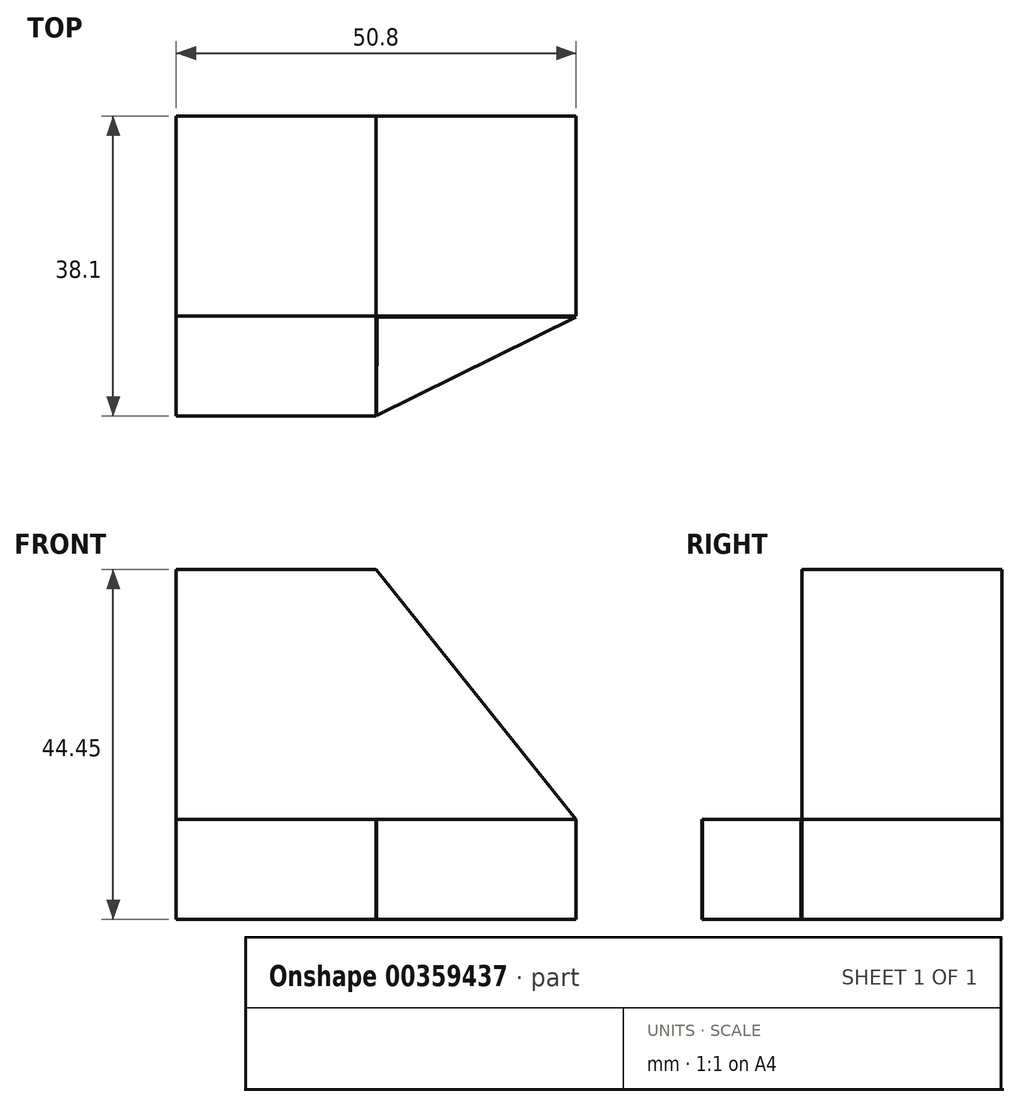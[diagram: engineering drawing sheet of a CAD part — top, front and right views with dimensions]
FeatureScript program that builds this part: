
annotation { "Feature Type Name" : "Feature", "Feature Type Description" : "" }
export const myFeature = defineFeature(function(context is Context, id is Id, definition is map)
    precondition{}
    {
        {
            var Q0;
            Q0=qCreatedBy(makeId("Front.planeOp"),FACE);
            var sketch = newSketch(context, id + "F0", { "sketchPlane" : qUnion([Q0])});
            skLineSegment(sketch, "E0", {"start": v(0, 12.7) * mm, "end": v(-25.4, 44.45) * mm});
            skLineSegment(sketch, "E1", {"start": v(-25.4, 44.45) * mm, "end": v(-50.8, 44.45) * mm});
            skLineSegment(sketch, "E2", {"start": v(-50.8, 44.45) * mm, "end": v(-50.8, 0) * mm});
            skLineSegment(sketch, "E3", {"start": v(-50.8, 0) * mm, "end": v(0, 0) * mm});
            skLineSegment(sketch, "E4", {"start": v(0, 0) * mm, "end": v(0, 12.7) * mm});
            skSolve(sketch);
        }
        {
            var Q0;
            Q0=makeQuery(id+"F0.imprint","IMPRINT",FACE,{"disambiguationData":[TD([[makeQuery(id+"F0.imprint","IMPRINT",EDGE,{"derivedFrom":sQuery(id+"F0.wireOp",EDGE,"E0")}),1.0]])]});
            extrude(context, id + "F1", {"entities" : qUnion([Q0]), "depth" : 25.4 * mm});
        }
        {
            var Q0;
            Q0=makeQuery(id+"F1.opExtrude","CAP_FACE",FACE,{"disambiguationData":[OSD([sQuery(id+"F0.wireOp",EDGE,"E0"),sQuery(id+"F0.wireOp",EDGE,"E1"),sQuery(id+"F0.wireOp",EDGE,"E2"),sQuery(id+"F0.wireOp",EDGE,"E3"),sQuery(id+"F0.wireOp",EDGE,"E4")])],"isStart":false});
            var sketch = newSketch(context, id + "F2", { "sketchPlane" : qUnion([Q0])});
            skLineSegment(sketch, "E5", {"start": v(-50.8, 0) * mm, "end": v(-25.4, 0) * mm});
            skLineSegment(sketch, "E6", {"start": v(-25.4, 0) * mm, "end": v(-25.4, 12.7) * mm});
            skLineSegment(sketch, "E7", {"start": v(-25.4, 12.7) * mm, "end": v(-50.8, 12.7) * mm});
            skLineSegment(sketch, "E8", {"start": v(-50.8, 12.7) * mm, "end": v(-50.8, 0) * mm});
            skSolve(sketch);
        }
        {
            var Q0;
            Q0=makeQuery(id+"F2.imprint","IMPRINT",FACE,{"disambiguationData":[TD([[makeQuery(id+"F2.imprint","IMPRINT",EDGE,{"derivedFrom":sQuery(id+"F2.wireOp",EDGE,"E5")}),1.0]])]});
            extrude(context, id + "F3", {"entities" : qUnion([Q0]), "operationType" : NewBodyOperationType.ADD, "depth" : 12.7 * mm});
        }
        {
            var Q0;
            Q0=qCreatedBy(makeId("Top.planeOp"),FACE);
            var sketch = newSketch(context, id + "F4", { "sketchPlane" : qUnion([Q0])});
            skLineSegment(sketch, "E9", {"start": v(-25.33, -38.04) * mm, "end": v(0, -25.51) * mm});
            skLineSegment(sketch, "E10", {"start": v(0, -25.51) * mm, "end": v(-25.27, -25.51) * mm});
            skLineSegment(sketch, "E11", {"start": v(-25.27, -25.51) * mm, "end": v(-25.33, -38.04) * mm});
            skSolve(sketch);
        }
        {
            var Q0;
            Q0 = qSketchRegion(id + "F4", true);
            extrude(context, id + "F5", {"entities" : qUnion([Q0]), "depth" : 12.7 * mm});
        }
    });
